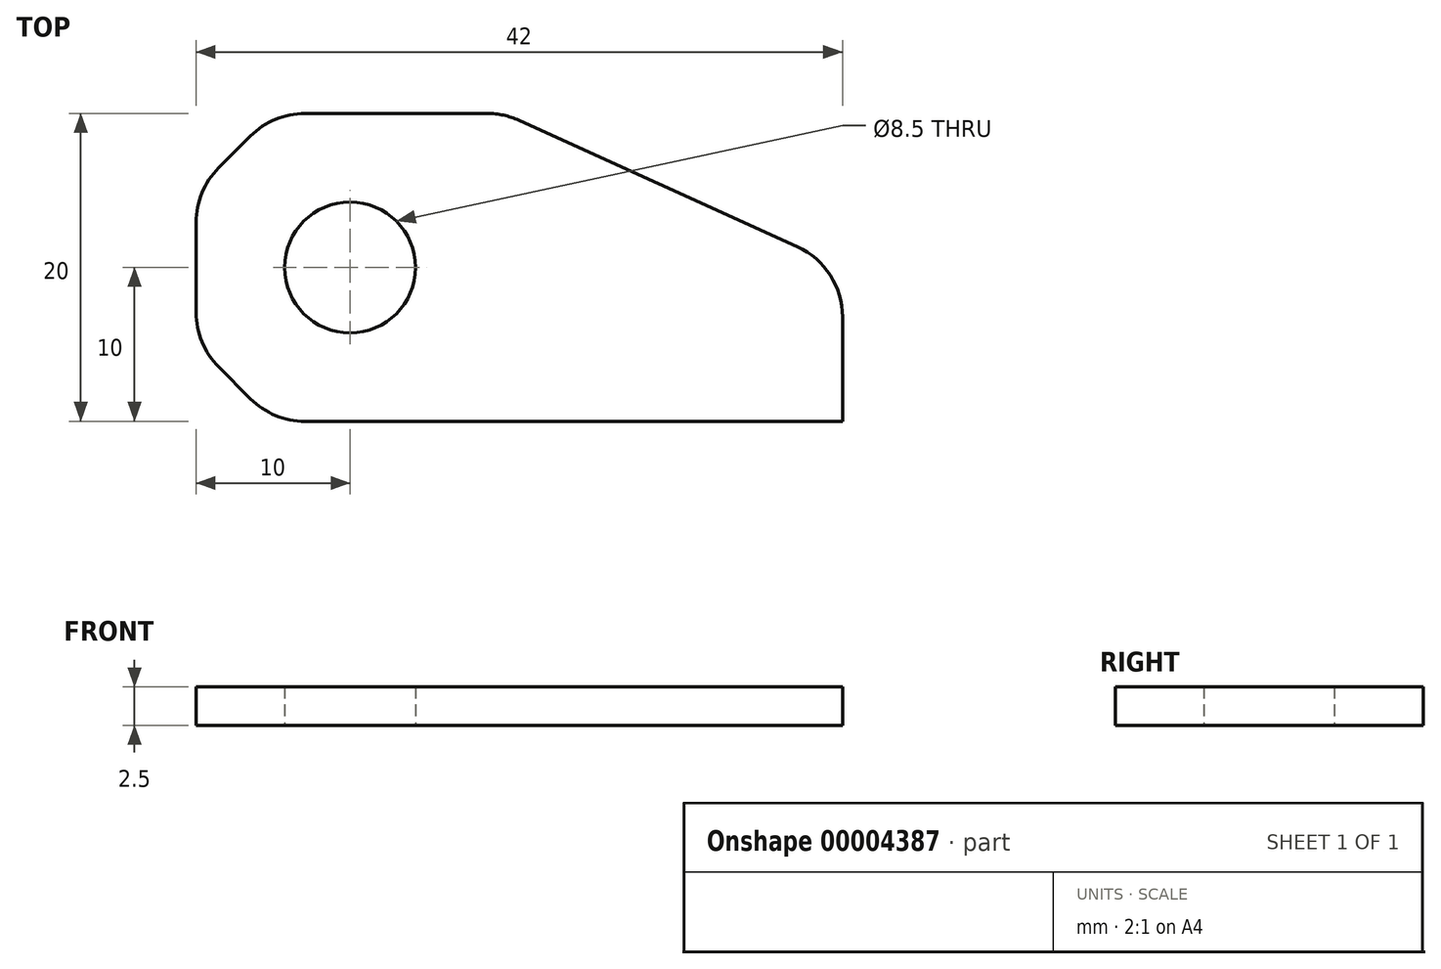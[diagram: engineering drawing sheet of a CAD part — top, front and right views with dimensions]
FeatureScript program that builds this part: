
annotation { "Feature Type Name" : "Feature", "Feature Type Description" : "" }
export const myFeature = defineFeature(function(context is Context, id is Id, definition is map)
    precondition{}
    {
        {
            var Q0;
            Q0=qCreatedBy(makeId("Top.planeOp"),FACE);
            var sketch = newSketch(context, id + "F0", { "sketchPlane" : qUnion([Q0])});
            skLineSegment(sketch, "E0.bottom", {"start": v(-5, 10) * mm, "end": v(10, 10) * mm});
            skLineSegment(sketch, "E0.top", {"start": v(-5, -10) * mm, "end": v(32, -10) * mm});
            skLineSegment(sketch, "E0.left", {"start": v(-10, 5) * mm, "end": v(-10, -5) * mm});
            skLineSegment(sketch, "E0.right", {"start": v(32, 0) * mm, "end": v(32, -10) * mm});
            skCircle(sketch, "E1", {"center": v(0, 0) * mm, "radius": 4.25 * mm});
            skLineSegment(sketch, "E2", {"start": v(-10, 5) * mm, "end": v(-5, 10) * mm});
            skLineSegment(sketch, "E3", {"start": v(-10, -5) * mm, "end": v(-5, -10) * mm});
            skLineSegment(sketch, "E4", {"start": v(10, 10) * mm, "end": v(32, 0) * mm});
            skPoint(sketch, "E5.orphan", {"position": v(32, 10) * mm});
            skSolve(sketch);
        }
        {
            var Q0;
            Q0 = qSketchRegion(id + "F0", true);
            extrude(context, id + "F1", {"entities" : qUnion([Q0]), "depth" : 2.5 * mm});
        }
        {
            var Q0;
            Q0=makeQuery(id+"F1.opExtrude","SWEPT_EDGE",EDGE,{"disambiguationData":[OSD([sQuery(id+"F0.wireOp",EDGE,"E0.top"),sQuery(id+"F0.wireOp",EDGE,"E3")])]});
            var Q1;
            Q1=makeQuery(id+"F1.opExtrude","SWEPT_EDGE",EDGE,{"disambiguationData":[OSD([sQuery(id+"F0.wireOp",EDGE,"E0.left"),sQuery(id+"F0.wireOp",EDGE,"E3")])]});
            var Q2;
            Q2=makeQuery(id+"F1.opExtrude","SWEPT_EDGE",EDGE,{"disambiguationData":[OSD([sQuery(id+"F0.wireOp",EDGE,"E0.left"),sQuery(id+"F0.wireOp",EDGE,"E2")])]});
            var Q3;
            Q3=makeQuery(id+"F1.opExtrude","SWEPT_EDGE",EDGE,{"disambiguationData":[OSD([sQuery(id+"F0.wireOp",EDGE,"E0.bottom"),sQuery(id+"F0.wireOp",EDGE,"E2")])]});
            var Q4;
            Q4=makeQuery(id+"F1.opExtrude","SWEPT_EDGE",EDGE,{"disambiguationData":[OSD([sQuery(id+"F0.wireOp",EDGE,"E0.bottom"),sQuery(id+"F0.wireOp",EDGE,"E4")])]});
            var Q5;
            Q5=makeQuery(id+"F1.opExtrude","SWEPT_EDGE",EDGE,{"disambiguationData":[OSD([sQuery(id+"F0.wireOp",EDGE,"E0.right"),sQuery(id+"F0.wireOp",EDGE,"E4")])]});
            fillet(context, id + "F2", {"entities" : qUnion([Q0, Q1, Q2, Q3, Q4, Q5]), "radius" : 5 * mm, "tangentPropagation" : true, "allowEdgeOverflow" : false});
        }
    });
